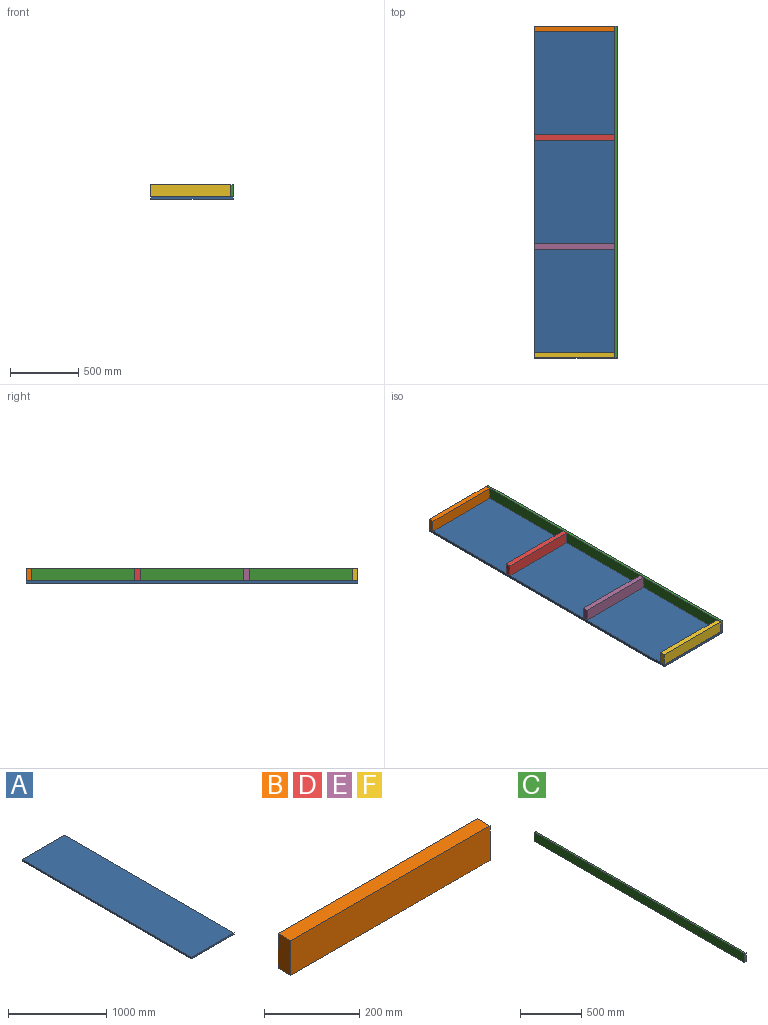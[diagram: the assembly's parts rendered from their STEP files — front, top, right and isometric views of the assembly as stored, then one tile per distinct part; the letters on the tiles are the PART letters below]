
ASSEMBLY  parts=6 mates=5
PART A: 6 faces, bbox 609.6x2438.4x19.1 mm
  f0: plane 2438.4x19.05mm, normal (-1,0,0), area 46451.5mm2, adj f1,f3,f4,f5
  f1: plane 609.6x19.05mm, normal (0,-1,0), area 11612.9mm2, adj f0,f2,f4,f5
  f2: plane 2438.4x19.05mm, normal (1,0,0), area 46451.5mm2, adj f1,f3,f4,f5
  f3: plane 609.6x19.05mm, normal (0,1,0), area 11612.9mm2, adj f0,f2,f4,f5
  f4: plane 2438.4x609.6mm, normal (0,0,1), area 1486448.6mm2, adj f0,f1,f2,f3
  f5: plane 2438.4x609.6mm, normal (0,0,-1), area 1486448.6mm2, adj f0,f1,f2,f3
PART B: 6 faces, bbox 590.6x38.1x88.9 mm
  f0: plane 590.55x88.9mm, normal (0,1,0), area 52499.9mm2, adj f1,f3,f4,f5
  f1: plane 88.9x38.1mm, normal (-1,0,0), area 3387.1mm2, adj f0,f2,f4,f5
  f2: plane 590.55x88.9mm, normal (0,-1,0), area 52499.9mm2, adj f1,f3,f4,f5
  f3: plane 88.9x38.1mm, normal (1,0,0), area 3387.1mm2, adj f0,f2,f4,f5
  f4: plane 590.55x38.1mm, normal (0,0,1), area 22500mm2, adj f0,f1,f2,f3
  f5: plane 590.55x38.1mm, normal (0,0,-1), area 22500mm2, adj f0,f1,f2,f3
PART C: 6 faces, bbox 19.1x2438.4x88.9 mm
  f0: plane 2438.4x19.05mm, normal (0,0,1), area 46451.5mm2, adj f1,f3,f4,f5
  f1: plane 88.9x19.05mm, normal (0,-1,0), area 1693.5mm2, adj f0,f2,f3,f4
  f2: plane 2438.4x19.05mm, normal (0,0,-1), area 46451.5mm2, adj f1,f3,f4,f5
  f3: plane 2438.4x88.9mm, normal (1,0,0), area 216773.8mm2, adj f0,f1,f2,f5
  f4: plane 2438.4x88.9mm, normal (-1,0,0), area 216773.8mm2, adj f0,f1,f2,f5
  f5: plane 88.9x19.05mm, normal (0,1,0), area 1693.5mm2, adj f0,f2,f3,f4
PART D: same geometry as B
PART E: same geometry as B
PART F: same geometry as B
PLACE A t=(-333.12,39.51,148.56)mm
PLACE B t=(-333.12,2477.91,167.61)mm
PLACE C t=(-27.42,-227.34,92.99)mm
PLACE D t=(-333.12,1677.81,167.61)mm
PLACE E t=(-333.12,877.71,167.61)mm
PLACE F t=(-333.12,77.61,167.61)mm
MATE fastened F.f1 <-> A.f0  axis (-1,0,0) through (-333.12,39.51,167.61)mm
MATE fastened B.f1 <-> A.f0  axis (-1,0,0) through (-333.12,2477.91,167.61)mm
MATE fastened E.f1 <-> F.f1  axis (-1,0,0) through (-333.12,839.61,167.61)mm
MATE fastened D.f1 <-> B.f1  axis (-1,0,0) through (-333.12,1677.81,167.61)mm
MATE fastened C.f3 <-> A.f2  axis (1,0,0) through (276.48,39.51,167.61)mm
